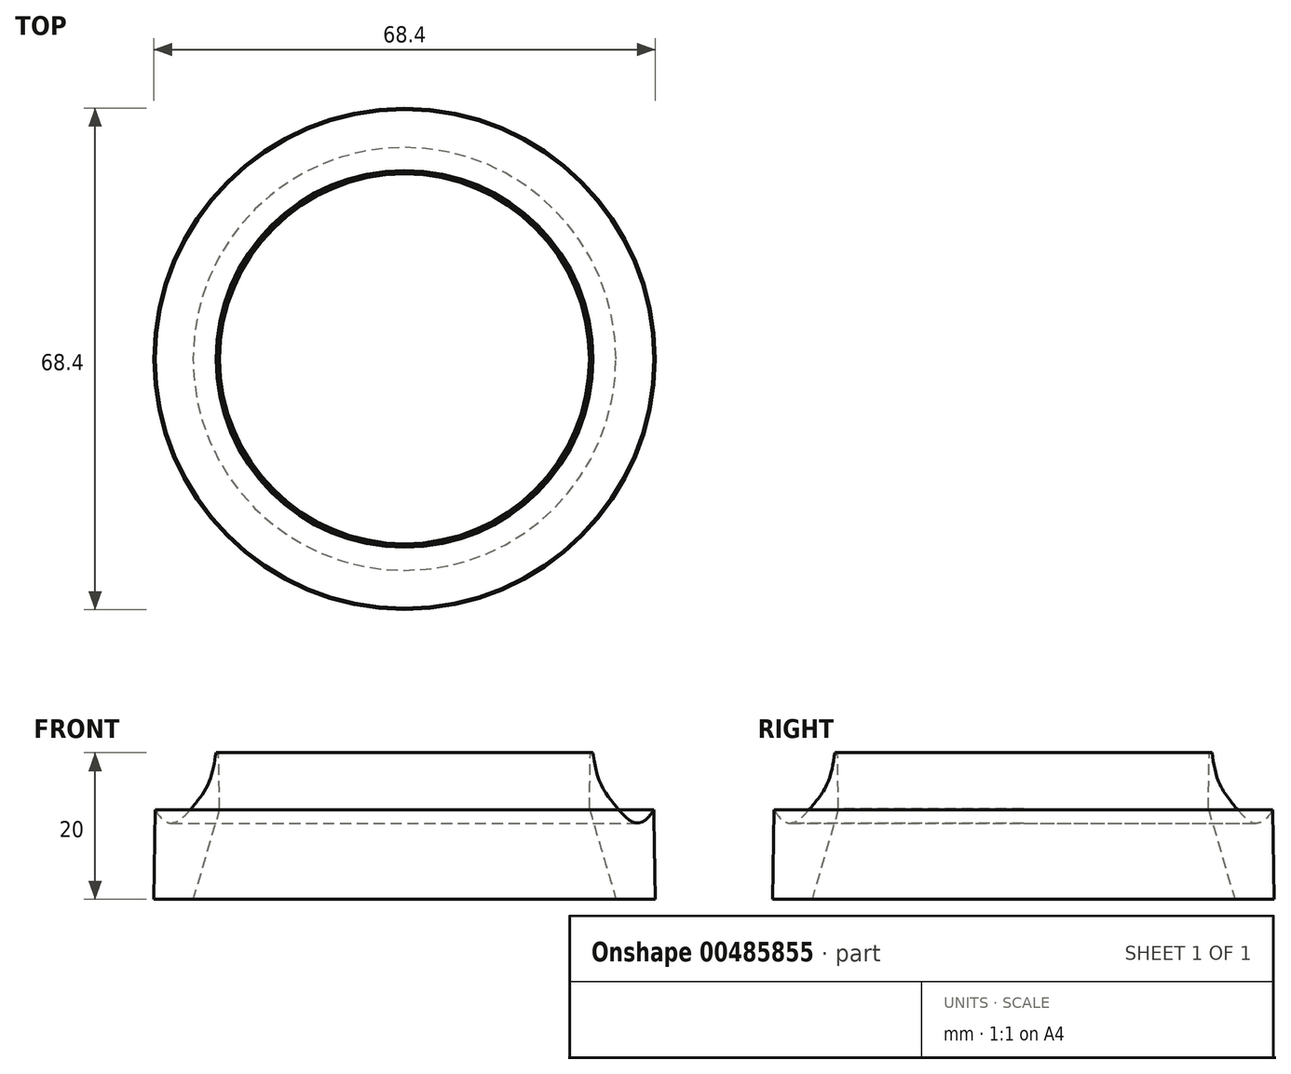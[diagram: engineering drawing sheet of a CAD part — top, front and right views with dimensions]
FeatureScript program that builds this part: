
annotation { "Feature Type Name" : "Feature", "Feature Type Description" : "" }
export const myFeature = defineFeature(function(context is Context, id is Id, definition is map)
    precondition{}
    {
        {
            var Q0;
            Q0=qCreatedBy(makeId("Top.planeOp"),FACE);
            var sketch = newSketch(context, id + "F0", { "sketchPlane" : qUnion([Q0])});
            skCircle(sketch, "E0", {"center": v(0, 0) * mm, "radius": 34.2 * mm});
            skCircle(sketch, "E1", {"center": v(0, 0) * mm, "radius": 25 * mm});
            skSolve(sketch);
        }
        {
            var Q0;
            Q0 = qSketchRegion(id + "F0", true);
            extrude(context, id + "F1", {"entities" : qUnion([Q0]), "depth" : 20 * mm, "hasDraft" : true, "draftAngle" : 1 * degree, "draftPullDirection" : true});
        }
        {
            var Q0;
            Q0=qCreatedBy(makeId("Front.planeOp"),FACE);
            var sketch = newSketch(context, id + "F2", { "sketchPlane" : qUnion([Q0])});
            skLineSegment(sketch, "E2", {"start": v(33.85, 20) * mm, "end": v(25.71, 20) * mm});
            skFitSpline(sketch, "E3", {"points": [v(33.85, 20) * mm, v(34.63, 13.75) * mm, v(31.95, 10.39) * mm, v(28.67, 12.88) * mm, v(25.71, 20) * mm], "startDerivative": vector(7.6, -32.07) * mm, "endDerivative": vector(-5.1, 41.8) * mm});
            skSolve(sketch);
        }
        {
            var Q0;
            Q0 = qSketchRegion(id + "F2", true);
            var Q1;
            Q1=makeQuery(id+"F1.opExtrude","CAP_EDGE",EDGE,{"disambiguationData":[OSD([sQuery(id+"F0.wireOp",EDGE,"E1")])],"isStart":false});
            revolve(context, id + "F3", {"operationType" : NewBodyOperationType.REMOVE, "entities" : qUnion([Q0]), "axis" : qUnion([Q1]), "revolveType" : RevolveType.FULL, "oppositeDirection" : true});
        }
        {
            var Q0;
            Q0=qCreatedBy(makeId("Front.planeOp"),FACE);
            var sketch = newSketch(context, id + "F4", { "sketchPlane" : qUnion([Q0])});
            skLineSegment(sketch, "E4", {"start": v(-28.83, 0) * mm, "end": v(-23.36, 18.64) * mm});
            skLineSegment(sketch, "E5", {"start": v(-23.36, 18.64) * mm, "end": v(-19, 0) * mm});
            skLineSegment(sketch, "E6", {"start": v(-19, 0) * mm, "end": v(-28.83, 0) * mm});
            skSolve(sketch);
        }
        {
            var Q0;
            Q0 = qSketchRegion(id + "F4", true);
            var Q1;
            {var subQ0=sQuery(id+"F2.wireOp",EDGE,"E3");var subQ1=sQuery(id+"F2.wireOp",EDGE,"E2");Q1=makeQuery(id+"F3.boolean.opBoolean","MERGE",EDGE,{"derivedFrom":[makeQuery(id+"F1.opExtrude","CAP_EDGE",EDGE,{"disambiguationData":[OSD([sQuery(id+"F0.wireOp",EDGE,"E1")])],"isStart":false}),makeQuery(id+"F3.opRevolve","SWEPT_EDGE",EDGE,{"disambiguationData":[OSD([subQ1,subQ0]),TDD([makeQuery(id+"F2.imprint","INTERSECT",VERTEX,{"disambiguationData":[OD(1.0)],"derivedFrom":[subQ1,subQ0]})])]})]});}
            revolve(context, id + "F5", {"operationType" : NewBodyOperationType.REMOVE, "entities" : qUnion([Q0]), "axis" : qUnion([Q1]), "revolveType" : RevolveType.FULL, "oppositeDirection" : true});
        }
    });
